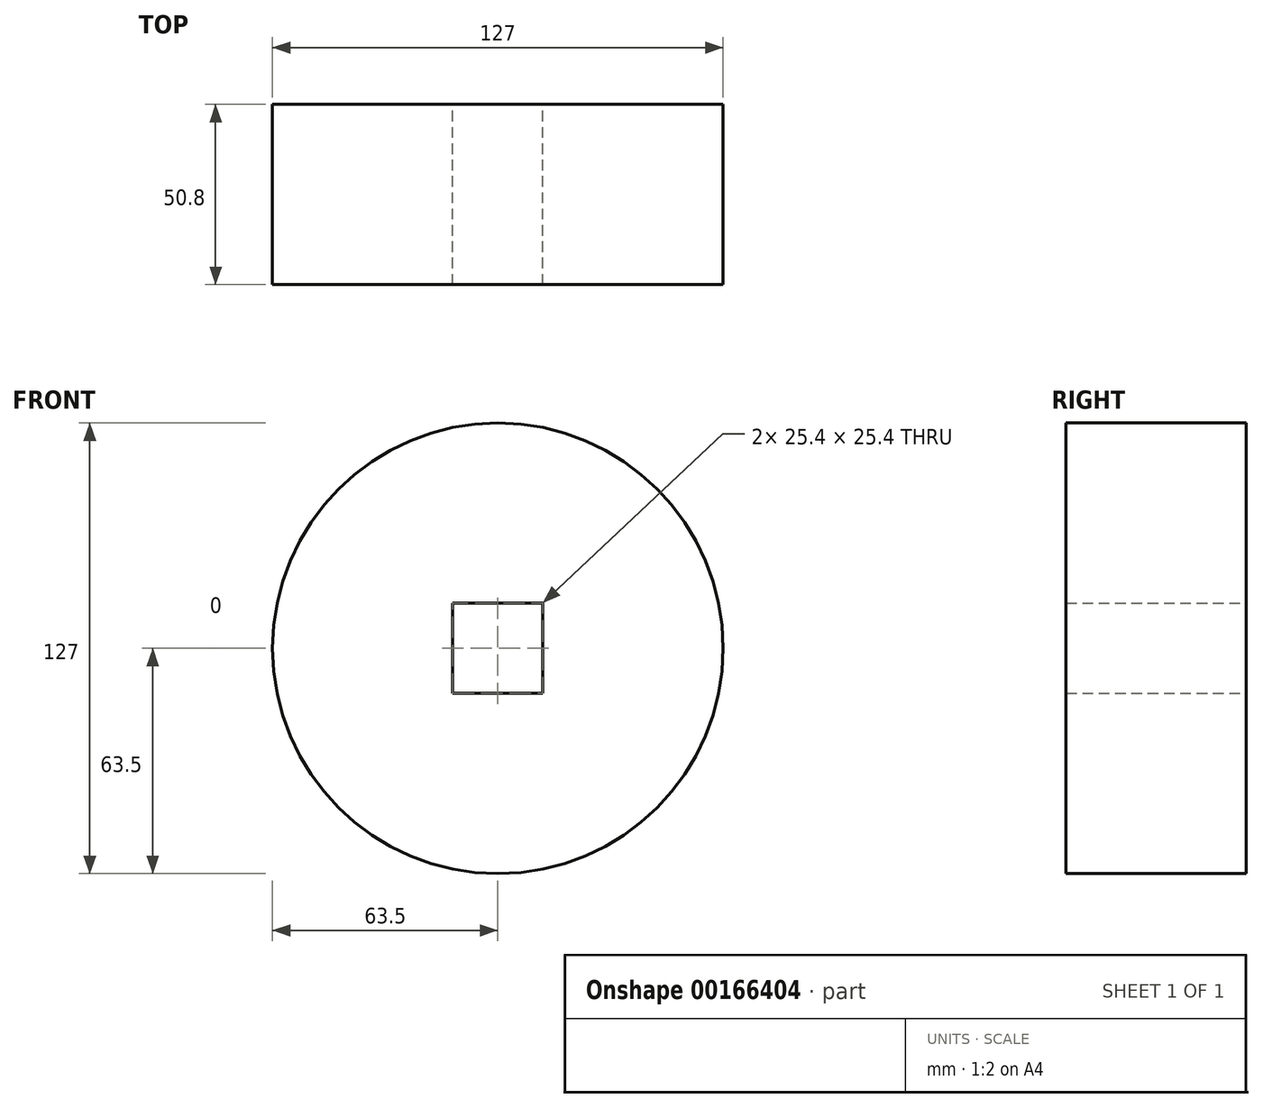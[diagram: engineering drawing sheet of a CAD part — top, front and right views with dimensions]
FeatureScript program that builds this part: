
annotation { "Feature Type Name" : "Feature", "Feature Type Description" : "" }
export const myFeature = defineFeature(function(context is Context, id is Id, definition is map)
    precondition{}
    {
        {
            var Q0;
            Q0=qCreatedBy(makeId("Front.planeOp"),FACE);
            var sketch = newSketch(context, id + "F0", { "sketchPlane" : qUnion([Q0])});
            skCircle(sketch, "E0", {"center": v(0, 0) * mm, "radius": 63.5 * mm});
            skLineSegment(sketch, "E1.bottom", {"start": v(12.7, -12.7) * mm, "end": v(-12.7, -12.7) * mm});
            skLineSegment(sketch, "E1.top", {"start": v(12.7, 12.7) * mm, "end": v(-12.7, 12.7) * mm});
            skLineSegment(sketch, "E1.left", {"start": v(12.7, -12.7) * mm, "end": v(12.7, 12.7) * mm});
            skLineSegment(sketch, "E1.right", {"start": v(-12.7, -12.7) * mm, "end": v(-12.7, 12.7) * mm});
            skSolve(sketch);
        }
        {
            var Q0;
            Q0=makeQuery(id+"F0.imprint","IMPRINT",FACE,{"disambiguationData":[TD([[makeQuery(id+"F0.imprint","IMPRINT",EDGE,{"derivedFrom":sQuery(id+"F0.wireOp",EDGE,"E0")}),1.0]])]});
            extrude(context, id + "F1", {"entities" : qUnion([Q0]), "depth" : 50.8 * mm});
        }
    });
